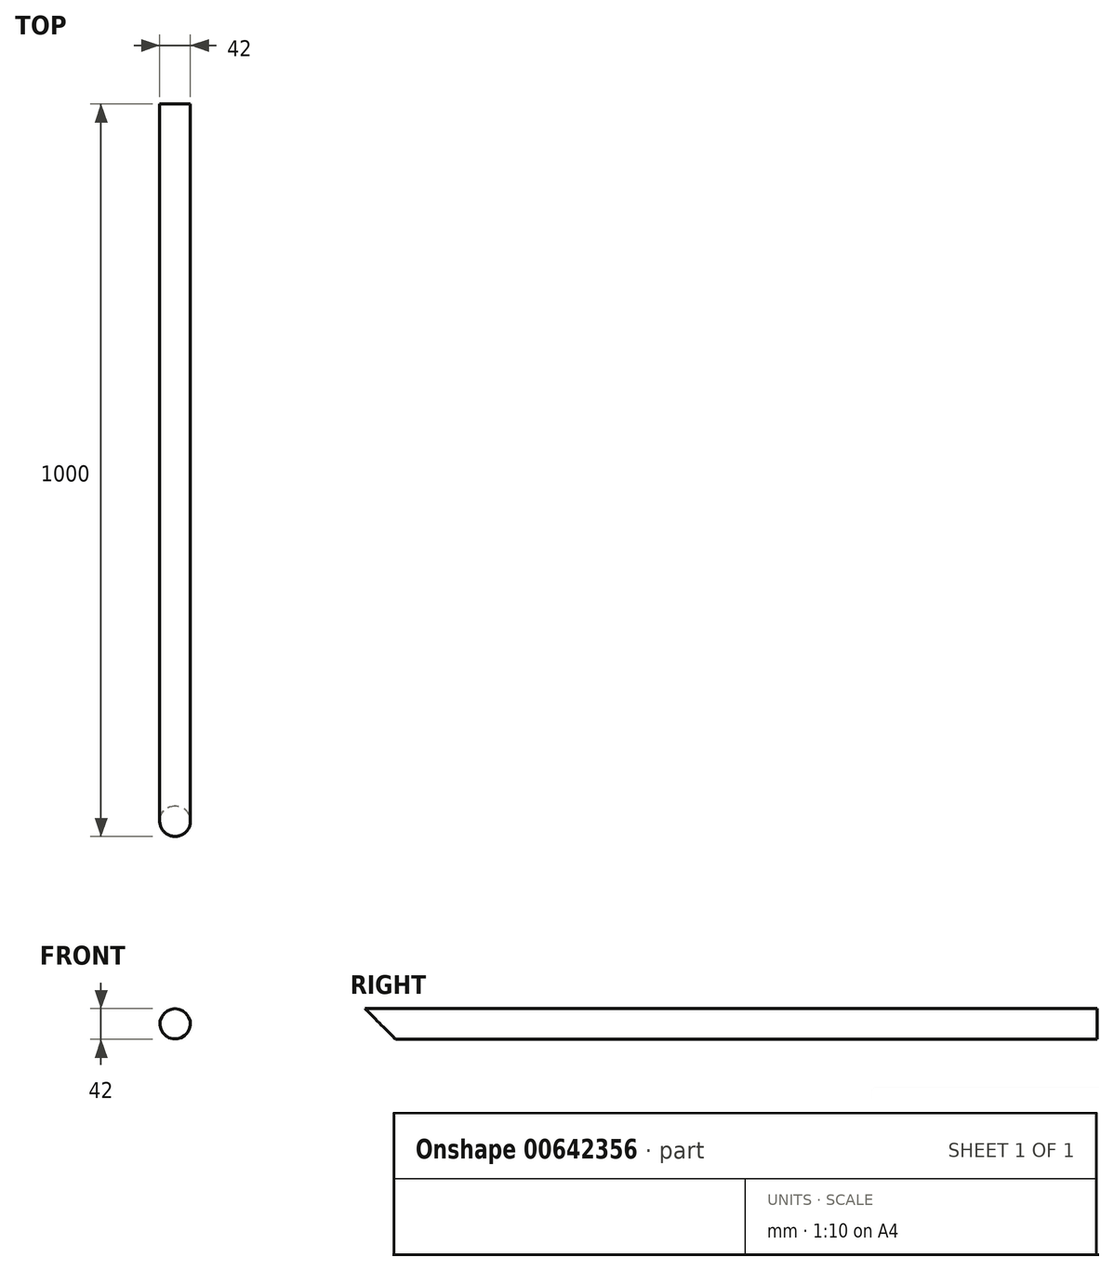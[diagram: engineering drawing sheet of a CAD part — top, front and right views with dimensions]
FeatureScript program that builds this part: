
annotation { "Feature Type Name" : "Feature", "Feature Type Description" : "" }
export const myFeature = defineFeature(function(context is Context, id is Id, definition is map)
    precondition{}
    {
        {
            var Q0;
            Q0=qCreatedBy(makeId("Front.planeOp"),FACE);
            var sketch = newSketch(context, id + "F0", { "sketchPlane" : qUnion([Q0])});
            skLineSegment(sketch, "E0.bottom", {"start": v(21, 21) * mm, "end": v(-21, 21) * mm});
            skLineSegment(sketch, "E0.top", {"start": v(21, -21) * mm, "end": v(-21, -21) * mm});
            skLineSegment(sketch, "E0.left", {"start": v(21, 21) * mm, "end": v(21, -21) * mm});
            skLineSegment(sketch, "E0.right", {"start": v(-21, 21) * mm, "end": v(-21, -21) * mm});
            skPoint(sketch, "E0.middle", {"position": v(0, 0) * mm});
            skSolve(sketch);
        }
        {
            var Q0;
            Q0=makeQuery(id+"F0.imprint","IMPRINT",FACE,{"disambiguationData":[TD([[makeQuery(id+"F0.imprint","IMPRINT",EDGE,{"derivedFrom":sQuery(id+"F0.wireOp",EDGE,"E0.bottom")}),1.0]])]});
            extrude(context, id + "F1", {"entities" : qUnion([Q0]), "depth" : 1000 * mm, "offsetDistance" : 25 * mm});
        }
        {
            var Q0;
            Q0=makeQuery(id+"F1.opExtrude","SWEPT_FACE",FACE,{"disambiguationData":[OSD([sQuery(id+"F0.wireOp",EDGE,"E0.left")])]});
            var sketch = newSketch(context, id + "F2", { "sketchPlane" : qUnion([Q0])});
            skLineSegment(sketch, "E1", {"start": v(-1000, 21) * mm, "end": v(-958, -21) * mm});
            skSolve(sketch);
        }
        {
            var Q0;
            {var subQ0=sQuery(id+"F2.wireOp",EDGE,"E1");Q0=makeQuery(id+"F2.imprint","IMPRINT",FACE,{"disambiguationData":[TD([[makeQuery(id+"F2.imprint","IMPRINT",EDGE,{"derivedFrom":subQ0}),-1.0]])]});}
            extrude(context, id + "F3", {"entities" : qUnion([Q0]), "operationType" : NewBodyOperationType.REMOVE, "oppositeDirection" : true, "depth" : 100 * mm, "offsetDistance" : 25 * mm});
        }
        {
            var Q0;
            Q0=makeQuery(id+"F1.opExtrude","SWEPT_EDGE",EDGE,{"disambiguationData":[OSD([sQuery(id+"F0.wireOp",EDGE,"E0.bottom"),sQuery(id+"F0.wireOp",EDGE,"E0.left")])]});
            var Q1;
            Q1=makeQuery(id+"F1.opExtrude","SWEPT_EDGE",EDGE,{"disambiguationData":[OSD([sQuery(id+"F0.wireOp",EDGE,"E0.top"),sQuery(id+"F0.wireOp",EDGE,"E0.left")])]});
            var Q2;
            Q2=makeQuery(id+"F1.opExtrude","SWEPT_EDGE",EDGE,{"disambiguationData":[OSD([sQuery(id+"F0.wireOp",EDGE,"E0.top"),sQuery(id+"F0.wireOp",EDGE,"E0.right")])]});
            var Q3;
            Q3=makeQuery(id+"F1.opExtrude","SWEPT_EDGE",EDGE,{"disambiguationData":[OSD([sQuery(id+"F0.wireOp",EDGE,"E0.bottom"),sQuery(id+"F0.wireOp",EDGE,"E0.right")])]});
            fillet(context, id + "F4", {"entities" : qUnion([Q0, Q1, Q2, Q3]), "radius" : 21 * mm, "tangentPropagation" : true, "allowEdgeOverflow" : false});
        }
    });
